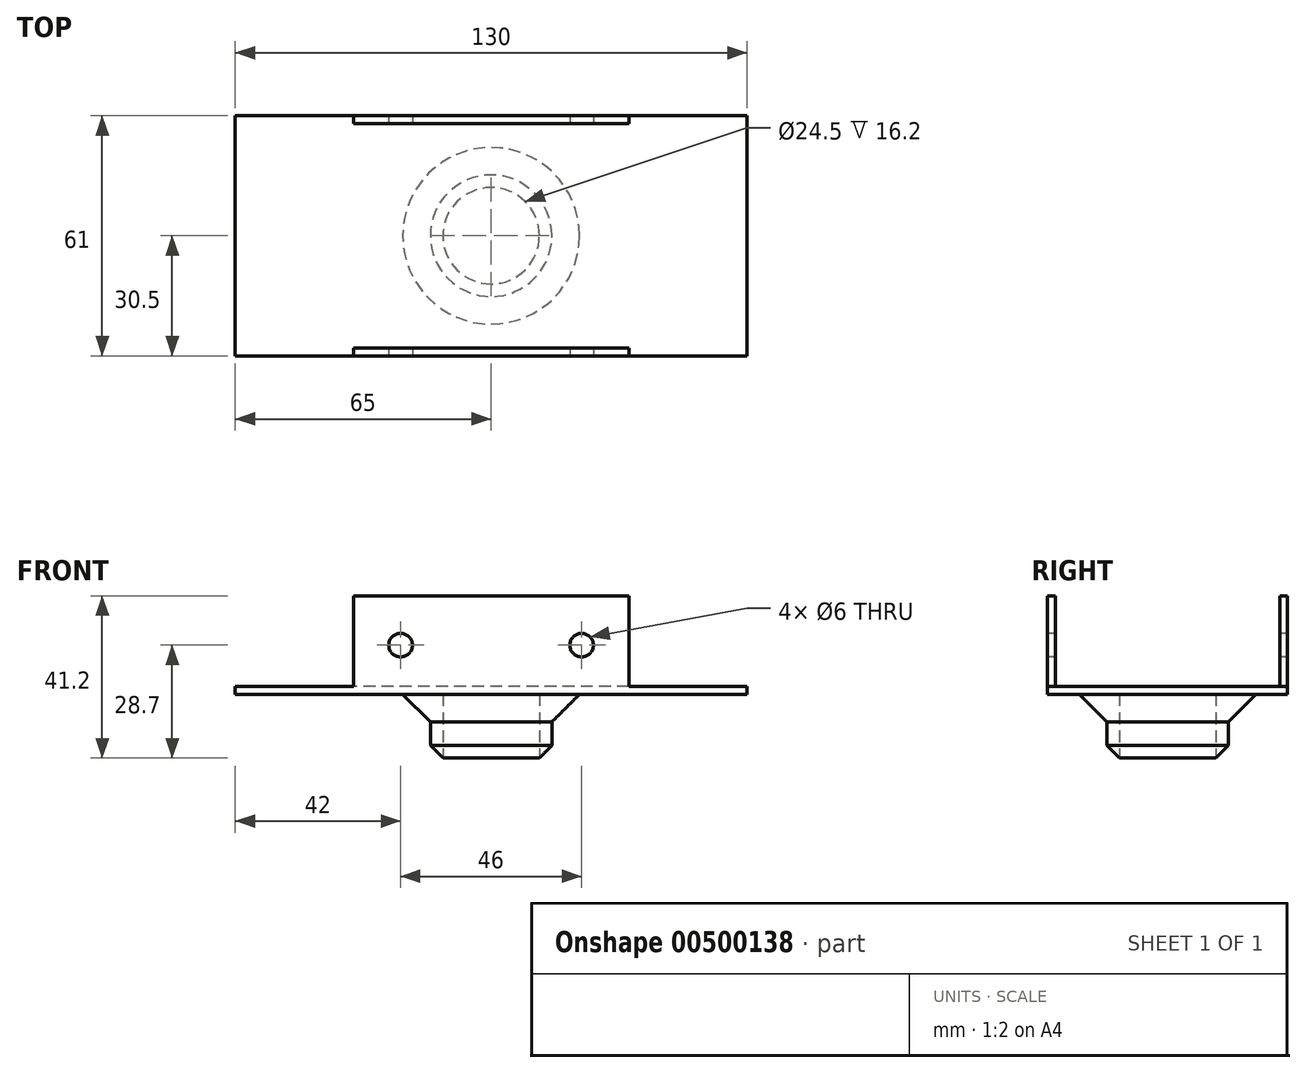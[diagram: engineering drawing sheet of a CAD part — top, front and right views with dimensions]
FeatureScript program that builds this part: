
annotation { "Feature Type Name" : "Feature", "Feature Type Description" : "" }
export const myFeature = defineFeature(function(context is Context, id is Id, definition is map)
    precondition{}
    {
        {
            var Q0;
            Q0=qCreatedBy(makeId("Top.planeOp"),FACE);
            var sketch = newSketch(context, id + "F0", { "sketchPlane" : qUnion([Q0])});
            skCircle(sketch, "E0", {"center": v(0, 0) * mm, "radius": 12.25 * mm});
            skCircle(sketch, "E1.0", {"center": v(0, 0) * mm, "radius": 15.45 * mm});
            skSolve(sketch);
        }
        {
            var Q0;
            Q0=makeQuery(id+"F0.imprint","IMPRINT",FACE,{"disambiguationData":[TD([[makeQuery(id+"F0.imprint","IMPRINT",EDGE,{"derivedFrom":sQuery(id+"F0.wireOp",EDGE,"E0")}),-1.0]])]});
            extrude(context, id + "F1", {"entities" : qUnion([Q0]), "depth" : 20 * mm});
        }
        {
            var Q0;
            Q0=makeQuery(id+"F1.opExtrude","CAP_FACE",FACE,{"disambiguationData":[OSD([sQuery(id+"F0.wireOp",EDGE,"E0"),sQuery(id+"F0.wireOp",EDGE,"E1.0")])],"isStart":false});
            var sketch = newSketch(context, id + "F2", { "sketchPlane" : qUnion([Q0])});
            skLineSegment(sketch, "E2.bottom", {"start": v(35, -28.5) * mm, "end": v(-35, -28.5) * mm});
            skLineSegment(sketch, "E2.top", {"start": v(35, 28.5) * mm, "end": v(-35, 28.5) * mm});
            skLineSegment(sketch, "E2.left", {"start": v(35, -28.5) * mm, "end": v(35, 28.5) * mm});
            skLineSegment(sketch, "E2.right", {"start": v(-35, -28.5) * mm, "end": v(-35, 28.5) * mm});
            skPoint(sketch, "E2.middle", {"position": v(0, 0) * mm});
            skSolve(sketch);
        }
        {
            var Q0;
            Q0 = qSketchRegion(id + "F2", true);
            extrude(context, id + "F3", {"entities" : qUnion([Q0]), "operationType" : NewBodyOperationType.ADD, "depth" : 2 * mm});
        }
        {
            var Q0;
            Q0=makeQuery(id+"F3.opExtrude","SWEPT_FACE",FACE,{"disambiguationData":[OSD([sQuery(id+"F2.wireOp",EDGE,"E2.bottom")])]});
            var sketch = newSketch(context, id + "F4", { "sketchPlane" : qUnion([Q0])});
            skLineSegment(sketch, "E3.bottom", {"start": v(-35, 20) * mm, "end": v(35, 20) * mm});
            skLineSegment(sketch, "E3.top", {"start": v(-35, 45) * mm, "end": v(35, 45) * mm});
            skLineSegment(sketch, "E3.left", {"start": v(-35, 20) * mm, "end": v(-35, 45) * mm});
            skLineSegment(sketch, "E3.right", {"start": v(35, 20) * mm, "end": v(35, 45) * mm});
            skSolve(sketch);
        }
        {
            var Q0;
            Q0 = qSketchRegion(id + "F4", true);
            extrude(context, id + "F5", {"entities" : qUnion([Q0]), "operationType" : NewBodyOperationType.ADD, "depth" : 2 * mm});
        }
        {
            var Q0;
            Q0=makeQuery(id+"F3.opExtrude","SWEPT_FACE",FACE,{"disambiguationData":[OSD([sQuery(id+"F2.wireOp",EDGE,"E2.top")])]});
            var sketch = newSketch(context, id + "F6", { "sketchPlane" : qUnion([Q0])});
            skLineSegment(sketch, "E4.bottom", {"start": v(-35, 20) * mm, "end": v(35, 20) * mm});
            skLineSegment(sketch, "E4.top", {"start": v(-35, 45) * mm, "end": v(35, 45) * mm});
            skLineSegment(sketch, "E4.left", {"start": v(-35, 20) * mm, "end": v(-35, 45) * mm});
            skLineSegment(sketch, "E4.right", {"start": v(35, 20) * mm, "end": v(35, 45) * mm});
            skSolve(sketch);
        }
        {
            var Q0;
            Q0 = qSketchRegion(id + "F6", true);
            extrude(context, id + "F7", {"entities" : qUnion([Q0]), "operationType" : NewBodyOperationType.ADD, "depth" : 2 * mm});
        }
        {
            var Q0;
            Q0=makeQuery(id+"F1.opExtrude","SWEPT_FACE",FACE,{"disambiguationData":[OSD([sQuery(id+"F0.wireOp",EDGE,"E1.0")])]});
            chamfer(context, id + "F8", {"entities" : qUnion([Q0]), "width" : 7 * mm, "tangentPropagation" : true});
        }
        {
            var Q0;
            Q0=makeQuery(id+"F5.opExtrude","CAP_FACE",FACE,{"disambiguationData":[OSD([sQuery(id+"F4.wireOp",EDGE,"E3.bottom"),sQuery(id+"F4.wireOp",EDGE,"E3.top"),sQuery(id+"F4.wireOp",EDGE,"E3.left"),sQuery(id+"F4.wireOp",EDGE,"E3.right")])],"isStart":false});
            var sketch = newSketch(context, id + "F9", { "sketchPlane" : qUnion([Q0])});
            skLineSegment(sketch, "E5", {"start": v(-35, 32.5) * mm, "end": v(35, 32.5) * mm, "construction": true});
            skCircle(sketch, "E6", {"center": v(-23, 32.5) * mm, "radius": 3 * mm});
            skCircle(sketch, "E7", {"center": v(23, 32.5) * mm, "radius": 3 * mm});
            skSolve(sketch);
        }
        {
            var Q0;
            Q0=sQuery(id+"F9.wireOp",VERTEX,"E6.center");
            var Q1;
            Q1=sQuery(id+"F9.wireOp",VERTEX,"E7.center");
            var Q2;
            Q2=makeQuery(id+"F1.opExtrude","SWEPT_BODY",BODY,{"disambiguationData":[OSD([sQuery(id+"F0.wireOp",EDGE,"E0"),sQuery(id+"F0.wireOp",EDGE,"E1.0")])]});
            hole(context, id + "F10", {"style" : HoleStyle.SIMPLE, "endStyle" : HoleEndStyle.THROUGH, "holeDiameter" : 6 * mm, "isTappedThrough" : true, "tappedDepth" : 12 * mm, "tapClearance" : 3, "locations" : qUnion([Q0, Q1]), "scope" : qUnion([Q2])});
        }
        {
            var Q0;
            Q0=makeQuery(id+"F7.boolean.opBoolean","MERGE",FACE,{"derivedFrom":[makeQuery(id+"F5.boolean.opBoolean","MERGE",FACE,{"derivedFrom":[makeQuery(id+"F3.opExtrude","SWEPT_FACE",FACE,{"disambiguationData":[OSD([sQuery(id+"F2.wireOp",EDGE,"E2.right")])]}),makeQuery(id+"F5.opExtrude","SWEPT_FACE",FACE,{"disambiguationData":[OSD([sQuery(id+"F4.wireOp",EDGE,"E3.left")])]})]}),makeQuery(id+"F7.opExtrude","SWEPT_FACE",FACE,{"disambiguationData":[OSD([sQuery(id+"F6.wireOp",EDGE,"E4.right")])]})]});
            var sketch = newSketch(context, id + "F11", { "sketchPlane" : qUnion([Q0])});
            skLineSegment(sketch, "E8.bottom", {"start": v(-30.5, 20) * mm, "end": v(30.5, 20) * mm});
            skLineSegment(sketch, "E8.top", {"start": v(-30.5, 22) * mm, "end": v(30.5, 22) * mm});
            skLineSegment(sketch, "E8.left", {"start": v(-30.5, 20) * mm, "end": v(-30.5, 22) * mm});
            skLineSegment(sketch, "E8.right", {"start": v(30.5, 20) * mm, "end": v(30.5, 22) * mm});
            skSolve(sketch);
        }
        {
            var Q0;
            Q0 = qSketchRegion(id + "F11", true);
            extrude(context, id + "F12", {"entities" : qUnion([Q0]), "operationType" : NewBodyOperationType.ADD, "depth" : 30 * mm});
        }
        {
            var Q0;
            Q0=makeQuery(id+"F7.boolean.opBoolean","MERGE",FACE,{"derivedFrom":[makeQuery(id+"F5.boolean.opBoolean","MERGE",FACE,{"derivedFrom":[makeQuery(id+"F3.opExtrude","SWEPT_FACE",FACE,{"disambiguationData":[OSD([sQuery(id+"F2.wireOp",EDGE,"E2.left")])]}),makeQuery(id+"F5.opExtrude","SWEPT_FACE",FACE,{"disambiguationData":[OSD([sQuery(id+"F4.wireOp",EDGE,"E3.right")])]})]}),makeQuery(id+"F7.opExtrude","SWEPT_FACE",FACE,{"disambiguationData":[OSD([sQuery(id+"F6.wireOp",EDGE,"E4.left")])]})]});
            var sketch = newSketch(context, id + "F13", { "sketchPlane" : qUnion([Q0])});
            skLineSegment(sketch, "E9.bottom", {"start": v(-30.5, 20) * mm, "end": v(30.5, 20) * mm});
            skLineSegment(sketch, "E9.top", {"start": v(-30.5, 22) * mm, "end": v(30.5, 22) * mm});
            skLineSegment(sketch, "E9.left", {"start": v(-30.5, 20) * mm, "end": v(-30.5, 22) * mm});
            skLineSegment(sketch, "E9.right", {"start": v(30.5, 20) * mm, "end": v(30.5, 22) * mm});
            skSolve(sketch);
        }
        {
            var Q0;
            Q0=makeQuery(id+"F13.imprint","IMPRINT",FACE,{"disambiguationData":[TD([[makeQuery(id+"F13.imprint","IMPRINT",EDGE,{"derivedFrom":sQuery(id+"F13.wireOp",EDGE,"E9.bottom")}),1.0]])]});
            extrude(context, id + "F14", {"entities" : qUnion([Q0]), "operationType" : NewBodyOperationType.ADD, "depth" : 30 * mm});
        }
    });
